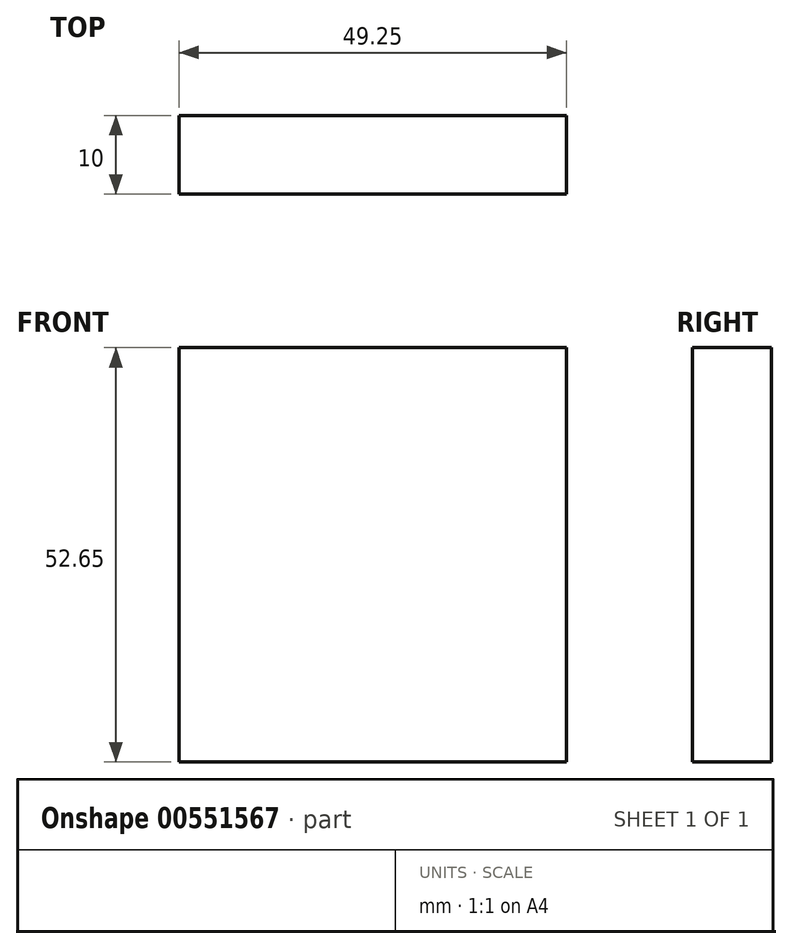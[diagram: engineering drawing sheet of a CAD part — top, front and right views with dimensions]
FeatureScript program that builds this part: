
annotation { "Feature Type Name" : "Feature", "Feature Type Description" : "" }
export const myFeature = defineFeature(function(context is Context, id is Id, definition is map)
    precondition{}
    {
        {
            var Q0;
            Q0=qCreatedBy(makeId("Front.planeOp"),FACE);
            var sketch = newSketch(context, id + "F0", { "sketchPlane" : qUnion([Q0])});
            skLineSegment(sketch, "E0.bottom", {"start": v(-49.25, 52.65) * mm, "end": v(0, 52.65) * mm});
            skLineSegment(sketch, "E0.top", {"start": v(-49.25, 0) * mm, "end": v(0, 0) * mm});
            skLineSegment(sketch, "E0.left", {"start": v(-49.25, 52.65) * mm, "end": v(-49.25, 0) * mm});
            skLineSegment(sketch, "E0.right", {"start": v(0, 52.65) * mm, "end": v(0, 0) * mm});
            skSolve(sketch);
        }
        {
            var Q0;
            Q0 = qSketchRegion(id + "F0", true);
            extrude(context, id + "F1", {"entities" : qUnion([Q0]), "depth" : 10 * mm, "offsetDistance" : 25.4 * mm});
        }
    });
